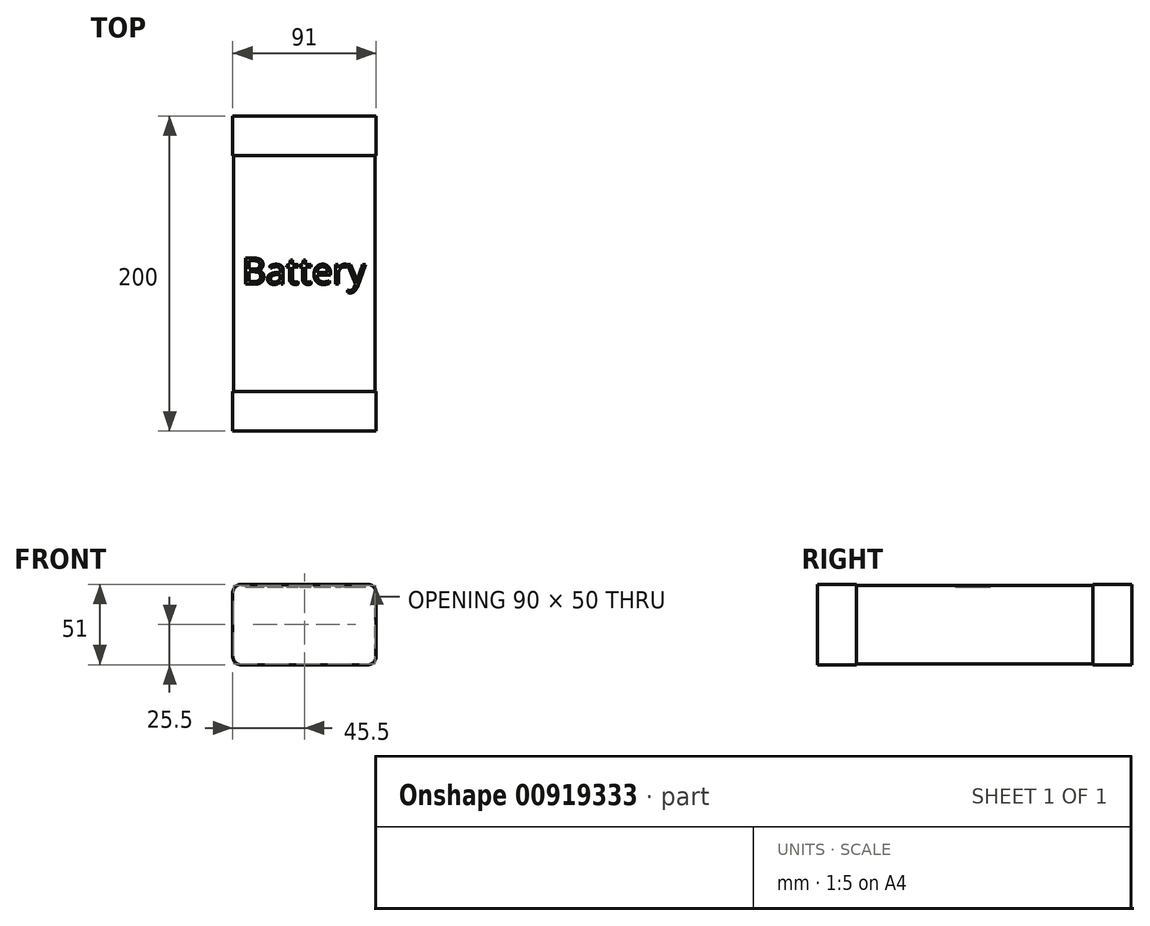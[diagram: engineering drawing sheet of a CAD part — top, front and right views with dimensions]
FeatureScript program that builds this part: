
annotation { "Feature Type Name" : "Feature", "Feature Type Description" : "" }
export const myFeature = defineFeature(function(context is Context, id is Id, definition is map)
    precondition{}
    {
        {
            var Q0;
            Q0=qCreatedBy(makeId("Front.planeOp"),FACE);
            var sketch = newSketch(context, id + "F0", { "sketchPlane" : qUnion([Q0])});
            skLineSegment(sketch, "E0.bottom", {"start": v(0, 0) * mm, "end": v(90, 0) * mm});
            skLineSegment(sketch, "E0.top", {"start": v(0, 50) * mm, "end": v(90, 50) * mm});
            skLineSegment(sketch, "E0.left", {"start": v(0, 0) * mm, "end": v(0, 50) * mm});
            skLineSegment(sketch, "E0.right", {"start": v(90, 0) * mm, "end": v(90, 50) * mm});
            skSolve(sketch);
        }
        {
            var Q0;
            Q0=makeQuery(id+"F0.imprint","IMPRINT",FACE,{"disambiguationData":[TD([[makeQuery(id+"F0.imprint","IMPRINT",EDGE,{"derivedFrom":sQuery(id+"F0.wireOp",EDGE,"E0.bottom")}),1.0]])]});
            extrude(context, id + "F1", {"entities" : qUnion([Q0]), "depth" : 200 * mm, "offsetDistance" : 25 * mm});
        }
        {
            var Q0;
            Q0=makeQuery(id+"F1.opExtrude","SWEPT_FACE",FACE,{"disambiguationData":[OSD([sQuery(id+"F0.wireOp",EDGE,"E0.top")])]});
            var sketch = newSketch(context, id + "F2", { "sketchPlane" : qUnion([Q0])});
            skText(sketch, "E1", { "text": "Battery\n", "fontName": "OpenSans-Regular.ttf"});
            const initialGuessF2  = {"E1": [0.0055, -0.1067, 1, 0, 0.0167]};
            skSetInitialGuess(sketch, initialGuessF2);
            skSolve(sketch);
        }
        {
            var Q0;
            Q0 = qSketchRegion(id + "F2", true);
            extrude(context, id + "F3", {"entities" : qUnion([Q0]), "operationType" : NewBodyOperationType.REMOVE, "oppositeDirection" : true, "depth" : 1 * mm, "offsetDistance" : 25 * mm});
        }
        {
            var Q0;
            Q0=makeQuery(id+"F1.opExtrude","CAP_FACE",FACE,{"disambiguationData":[OSD([sQuery(id+"F0.wireOp",EDGE,"E0.bottom"),sQuery(id+"F0.wireOp",EDGE,"E0.top"),sQuery(id+"F0.wireOp",EDGE,"E0.left"),sQuery(id+"F0.wireOp",EDGE,"E0.right")])],"isStart":false});
            var sketch = newSketch(context, id + "F4", { "sketchPlane" : qUnion([Q0])});
            skLineSegment(sketch, "E2.0", {"start": v(90.5, 50.5) * mm, "end": v(-0.5, 50.5) * mm});
            skLineSegment(sketch, "E2.1", {"start": v(90.5, -0.5) * mm, "end": v(90.5, 50.5) * mm});
            skLineSegment(sketch, "E2.2", {"start": v(-0.5, -0.5) * mm, "end": v(90.5, -0.5) * mm});
            skLineSegment(sketch, "E2.3", {"start": v(-0.5, 50.5) * mm, "end": v(-0.5, -0.5) * mm});
            skSolve(sketch);
        }
        {
            var Q0;
            Q0=makeQuery(id+"F4.imprint","IMPRINT",FACE,{"disambiguationData":[TD([[makeQuery(id+"F4.imprint","IMPRINT",EDGE,{"derivedFrom":sQuery(id+"F4.wireOp",EDGE,"E2.0")}),1.0]])]});
            extrude(context, id + "F5", {"entities" : qUnion([Q0]), "operationType" : NewBodyOperationType.ADD, "oppositeDirection" : true, "depth" : 25 * mm, "offsetDistance" : 25 * mm});
        }
        {
            var Q0;
            Q0=makeQuery(id+"F1.opExtrude","CAP_FACE",FACE,{"disambiguationData":[OSD([sQuery(id+"F0.wireOp",EDGE,"E0.bottom"),sQuery(id+"F0.wireOp",EDGE,"E0.top"),sQuery(id+"F0.wireOp",EDGE,"E0.left"),sQuery(id+"F0.wireOp",EDGE,"E0.right")])],"isStart":true});
            var sketch = newSketch(context, id + "F6", { "sketchPlane" : qUnion([Q0])});
            skLineSegment(sketch, "E3.0", {"start": v(0.5, 50.5) * mm, "end": v(-90.5, 50.5) * mm});
            skLineSegment(sketch, "E3.1", {"start": v(0.5, -0.5) * mm, "end": v(0.5, 50.5) * mm});
            skLineSegment(sketch, "E3.2", {"start": v(-90.5, -0.5) * mm, "end": v(0.5, -0.5) * mm});
            skLineSegment(sketch, "E3.3", {"start": v(-90.5, 50.5) * mm, "end": v(-90.5, -0.5) * mm});
            skSolve(sketch);
        }
        {
            var Q0;
            Q0=makeQuery(id+"F6.imprint","IMPRINT",FACE,{"disambiguationData":[TD([[makeQuery(id+"F6.imprint","IMPRINT",EDGE,{"derivedFrom":sQuery(id+"F6.wireOp",EDGE,"E3.0")}),1.0]])]});
            extrude(context, id + "F7", {"entities" : qUnion([Q0]), "operationType" : NewBodyOperationType.ADD, "oppositeDirection" : true, "depth" : 25 * mm, "offsetDistance" : 25 * mm});
        }
        {
            var Q0;
            Q0=makeQuery(id+"F1.opExtrude","SWEPT_EDGE",EDGE,{"disambiguationData":[OSD([sQuery(id+"F0.wireOp",EDGE,"E0.top"),sQuery(id+"F0.wireOp",EDGE,"E0.right")])]});
            var Q1;
            Q1=makeQuery(id+"F1.opExtrude","SWEPT_EDGE",EDGE,{"disambiguationData":[OSD([sQuery(id+"F0.wireOp",EDGE,"E0.top"),sQuery(id+"F0.wireOp",EDGE,"E0.left")])]});
            var Q2;
            Q2=makeQuery(id+"F1.opExtrude","SWEPT_EDGE",EDGE,{"disambiguationData":[OSD([sQuery(id+"F0.wireOp",EDGE,"E0.bottom"),sQuery(id+"F0.wireOp",EDGE,"E0.right")])]});
            var Q3;
            Q3=makeQuery(id+"F1.opExtrude","SWEPT_EDGE",EDGE,{"disambiguationData":[OSD([sQuery(id+"F0.wireOp",EDGE,"E0.bottom"),sQuery(id+"F0.wireOp",EDGE,"E0.left")])]});
            var Q4;
            Q4=makeQuery(id+"F7.opExtrude","SWEPT_EDGE",EDGE,{"disambiguationData":[OSD([sQuery(id+"F6.wireOp",EDGE,"E3.0"),sQuery(id+"F6.wireOp",EDGE,"E3.3")])]});
            var Q5;
            Q5=makeQuery(id+"F7.opExtrude","SWEPT_EDGE",EDGE,{"disambiguationData":[OSD([sQuery(id+"F6.wireOp",EDGE,"E3.0"),sQuery(id+"F6.wireOp",EDGE,"E3.1")])]});
            var Q6;
            Q6=makeQuery(id+"F7.opExtrude","SWEPT_EDGE",EDGE,{"disambiguationData":[OSD([sQuery(id+"F6.wireOp",EDGE,"E3.2"),sQuery(id+"F6.wireOp",EDGE,"E3.3")])]});
            var Q7;
            Q7=makeQuery(id+"F7.opExtrude","SWEPT_EDGE",EDGE,{"disambiguationData":[OSD([sQuery(id+"F6.wireOp",EDGE,"E3.1"),sQuery(id+"F6.wireOp",EDGE,"E3.2")])]});
            var Q8;
            Q8=makeQuery(id+"F5.opExtrude","SWEPT_EDGE",EDGE,{"disambiguationData":[OSD([sQuery(id+"F4.wireOp",EDGE,"E2.0"),sQuery(id+"F4.wireOp",EDGE,"E2.3")])]});
            var Q9;
            Q9=makeQuery(id+"F5.opExtrude","SWEPT_EDGE",EDGE,{"disambiguationData":[OSD([sQuery(id+"F4.wireOp",EDGE,"E2.2"),sQuery(id+"F4.wireOp",EDGE,"E2.3")])]});
            var Q10;
            Q10=makeQuery(id+"F5.opExtrude","SWEPT_EDGE",EDGE,{"disambiguationData":[OSD([sQuery(id+"F4.wireOp",EDGE,"E2.0"),sQuery(id+"F4.wireOp",EDGE,"E2.1")])]});
            var Q11;
            Q11=makeQuery(id+"F5.opExtrude","SWEPT_EDGE",EDGE,{"disambiguationData":[OSD([sQuery(id+"F4.wireOp",EDGE,"E2.1"),sQuery(id+"F4.wireOp",EDGE,"E2.2")])]});
            fillet(context, id + "F8", {"entities" : qUnion([Q0, Q1, Q2, Q3, Q4, Q5, Q6, Q7, Q8, Q9, Q10, Q11]), "radius" : 5 * mm, "tangentPropagation" : true, "allowEdgeOverflow" : false});
        }
    });
